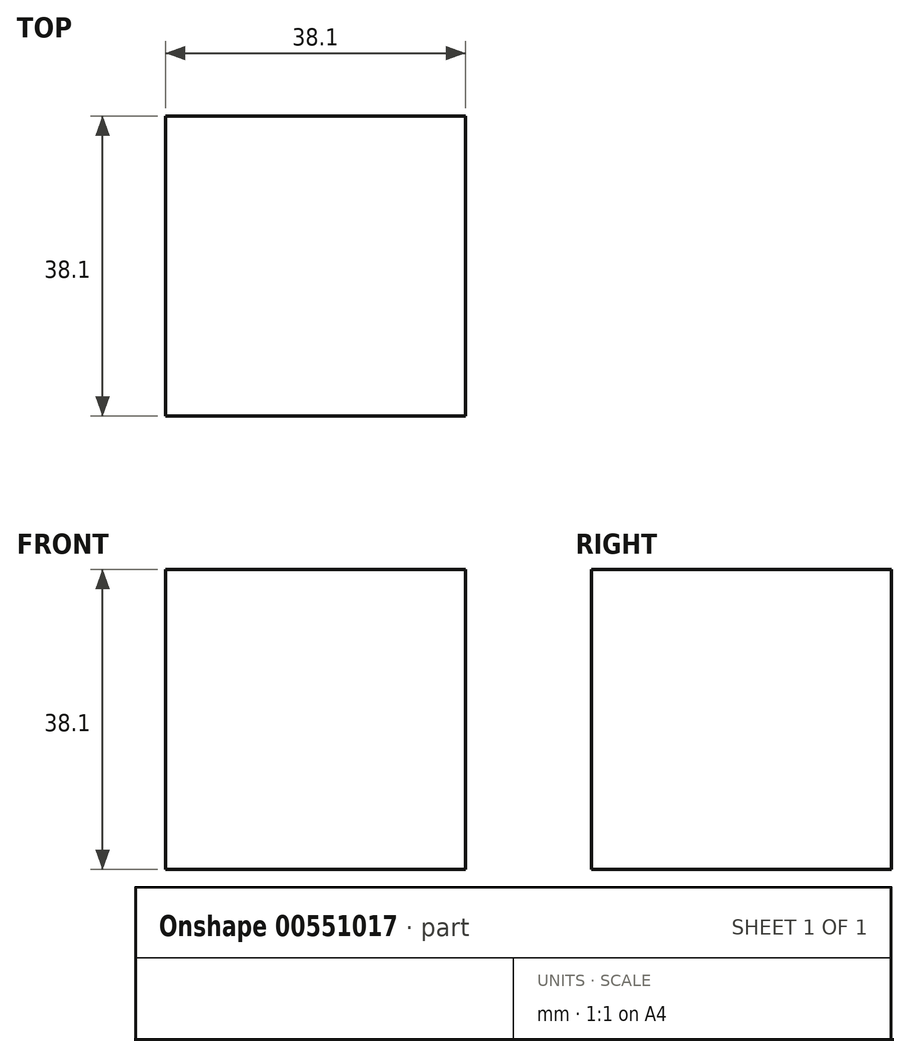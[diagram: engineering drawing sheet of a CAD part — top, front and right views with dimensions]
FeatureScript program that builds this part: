
annotation { "Feature Type Name" : "Feature", "Feature Type Description" : "" }
export const myFeature = defineFeature(function(context is Context, id is Id, definition is map)
    precondition{}
    {
        {
            var Q0;
            Q0=qCreatedBy(makeId("Right.planeOp"),FACE);
            var sketch = newSketch(context, id + "F0", { "sketchPlane" : qUnion([Q0])});
            skLineSegment(sketch, "E0", {"start": v(0, 38.1) * mm, "end": v(-38.1, 38.1) * mm});
            skLineSegment(sketch, "E1", {"start": v(-38.1, 38.1) * mm, "end": v(-38.1, 0) * mm});
            skLineSegment(sketch, "E2", {"start": v(0, 38.1) * mm, "end": v(0, 29.2) * mm});
            skLineSegment(sketch, "E3", {"start": v(0, 0) * mm, "end": v(-38.1, 0) * mm});
            skLineSegment(sketch, "E4", {"start": v(-38.1, 38.1) * mm, "end": v(0, 38.1) * mm});
            skPoint(sketch, "E5.orphan", {"position": v(-76.27, 38.1) * mm});
            skPoint(sketch, "E6.start.orphan", {"position": v(0, 29.2) * mm});
            skPoint(sketch, "E7.start.orphan", {"position": v(-29.21, 29.2) * mm});
            skPoint(sketch, "E8.end.orphan", {"position": v(0, 8.9) * mm});
            skLineSegment(sketch, "E9.trimOffspring", {"start": v(0, 8.9) * mm, "end": v(0, 0) * mm});
            skLineSegment(sketch, "E10", {"start": v(0, 29.2) * mm, "end": v(0, 8.9) * mm});
            skLineSegment(sketch, "E11", {"start": v(-29.21, 29.2) * mm, "end": v(0, 29.2) * mm});
            skLineSegment(sketch, "E12", {"start": v(0, 8.9) * mm, "end": v(-29.21, 8.9) * mm});
            skLineSegment(sketch, "E13", {"start": v(-29.21, 8.9) * mm, "end": v(-29.21, 29.2) * mm});
            skSolve(sketch);
        }
        {
            var Q0;
            Q0 = qSketchRegion(id + "F0", true);
            extrude(context, id + "F1", {"entities" : qUnion([Q0]), "depth" : 38.1 * mm, "offsetDistance" : 25.4 * mm});
        }
        {
            var Q0;
            Q0=makeQuery(id+"F0.imprint","IMPRINT",FACE,{"disambiguationData":[TD([[makeQuery(id+"F0.imprint","IMPRINT",EDGE,{"derivedFrom":sQuery(id+"F0.wireOp",EDGE,"E10")}),-1.0]])]});
            extrude(context, id + "F2", {"entities" : qUnion([Q0]), "operationType" : NewBodyOperationType.REMOVE, "oppositeDirection" : true, "depth" : 38.1 * mm, "offsetDistance" : 25.4 * mm});
        }
    });
